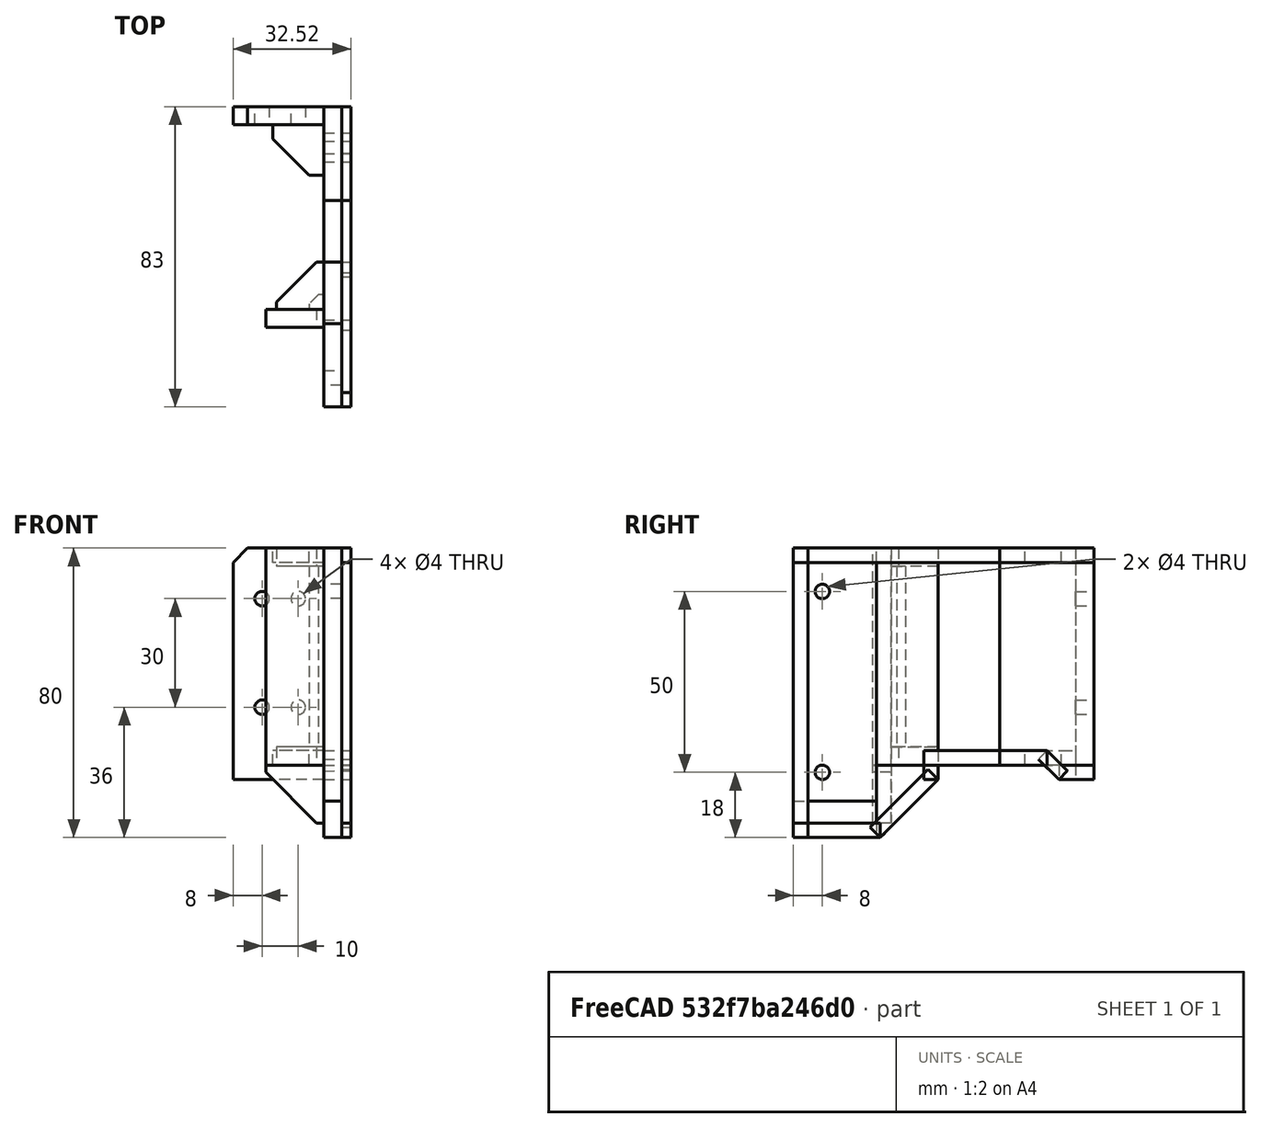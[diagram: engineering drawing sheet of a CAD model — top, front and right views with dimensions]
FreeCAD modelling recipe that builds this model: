
FCSTD DOCUMENT  (FreeCAD 0.20R29410 (Git))
Label: main_01
License: All rights reserved
LicenseURL: http://en.wikipedia.org/wiki/All_rights_reserved
objects: Part::Part2DObjectPython×33, Part::Extrusion×30, Part::Chamfer×8, Part::Cut×6
note: 77 computed .brp shape members not serialized (recipe doc carries the construction recipe); baked Part::Feature solids carry a one-line shape summary decoded from their .brp

FEATURE [Part::Part2DObjectPython] Rectangle  # Draft 2D object (typed FeaturePython)
  Area = 0
  ChamferSize = 0
  Columns = 1
  FilletRadius = 0
  Height = 70
  Length = 23
  MakeFace = false
  Placement = pos=(0,-40,0) rot=(0.57735,0.57735,0.57735;2.0944rad)
  Rows = 1
FEATURE [Part::Part2DObjectPython] Circle  # Draft 2D object (typed FeaturePython)
  Area = 0
  FirstAngle = 0
  LastAngle = 0
  MakeFace = false
  Placement = pos=(0,-32,58) rot=(0.57735,0.57735,0.57735;2.0944rad)
  Radius = 4
FEATURE [Part::Part2DObjectPython] Circle001  # Draft 2D object (typed FeaturePython)
  Area = 0
  FirstAngle = 0
  LastAngle = 0
  MakeFace = false
  Placement = pos=(0,-32,8) rot=(0.57735,0.57735,0.57735;2.0944rad)
  Radius = 4
FEATURE [Part::Part2DObjectPython] Rectangle001  # Draft 2D object (typed FeaturePython)
  Area = 0
  ChamferSize = 0
  Columns = 1
  FilletRadius = 0
  Height = 10
  Length = 23
  MakeFace = false
  Placement = pos=(0,-40,-10) rot=(0.57735,0.57735,0.57735;2.0944rad)
  Rows = 1
FEATURE [Part::Part2DObjectPython] Rectangle002  # Draft 2D object (typed FeaturePython)
  Area = 0
  ChamferSize = 0
  Columns = 1
  FilletRadius = 0
  Height = 20
  Length = 17
  MakeFace = false
  Placement = pos=(0,-17,-10) rot=(0.57735,0.57735,0.57735;2.0944rad)
  Rows = 1
FEATURE [Part::Part2DObjectPython] Rectangle003  # Draft 2D object (typed FeaturePython)
  Area = 0
  ChamferSize = 0
  Columns = 1
  FilletRadius = 0
  Height = 60
  Length = 17
  MakeFace = false
  Placement = pos=(0,0,10) rot=(0.57735,0.57735,0.57735;2.0944rad)
  Rows = 1
FEATURE [Part::Part2DObjectPython] Rectangle004  # Draft 2D object (typed FeaturePython)
  Area = 0
  ChamferSize = 0
  Columns = 1
  FilletRadius = 0
  Height = 60
  Length = 17
  MakeFace = false
  Placement = pos=(0,-17,10) rot=(0.57735,0.57735,0.57735;2.0944rad)
  Rows = 1
FEATURE [Part::Extrusion] Extrude
  Base = -> Rectangle
  Dir = (1,-2e-16,2e-16)
  DirMode = 2
  FaceMakerClass = Part::FaceMakerBullseye
  LengthFwd = 5
  LengthRev = 0
  Solid = true
  Symmetric = false
FEATURE [Part::Extrusion] Extrude001
  Base = -> Rectangle004
  Dir = (1,0,0)
  DirMode = 2
  FaceMakerClass = Part::FaceMakerBullseye
  LengthFwd = 5
  LengthRev = 0
  Solid = true
  Symmetric = false
FEATURE [Part::Extrusion] Extrude002
  Base = -> Rectangle003
  Dir = (1,-2e-16,2e-16)
  DirMode = 2
  FaceMakerClass = Part::FaceMakerBullseye
  LengthFwd = 5
  LengthRev = 0
  Solid = true
  Symmetric = false
FEATURE [Part::Extrusion] Extrude003
  Base = -> Rectangle001
  Dir = (1,-2e-16,2e-16)
  DirMode = 2
  FaceMakerClass = Part::FaceMakerBullseye
  LengthFwd = 5
  LengthRev = 0
  Solid = true
  Symmetric = false
FEATURE [Part::Extrusion] Extrude004
  Base = -> Rectangle002
  Dir = (1,-2e-16,2e-16)
  DirMode = 2
  FaceMakerClass = Part::FaceMakerBullseye
  LengthFwd = 5
  LengthRev = 0
  Solid = true
  Symmetric = false
FEATURE [Part::Chamfer] Chamfer
  Base = -> Extrude004
  Edges = 1 edges r=16: [Edge2]
FEATURE [Part::Part2DObjectPython] Rectangle005  # Draft 2D object (typed FeaturePython)
  Area = 0
  ChamferSize = 0
  Columns = 1
  FilletRadius = 0
  Height = 4
  Length = 57
  MakeFace = false
  Placement = pos=(5,-40,66) rot=(0.57735,0.57735,0.57735;2.0944rad)
  Rows = 1
FEATURE [Part::Part2DObjectPython] Rectangle006  # Draft 2D object (typed FeaturePython)
  Area = 0
  ChamferSize = 0
  Columns = 1
  FilletRadius = 0
  Height = 80
  Length = 4
  MakeFace = false
  Placement = pos=(5,-40,-10) rot=(0.57735,0.57735,0.57735;2.0944rad)
  Rows = 1
FEATURE [Part::Part2DObjectPython] Rectangle007  # Draft 2D object (typed FeaturePython)
  Area = 0
  ChamferSize = 0
  Columns = 1
  FilletRadius = 0
  Height = 4
  Length = 24
  MakeFace = false
  Placement = pos=(5,-40,-10) rot=(0.57735,0.57735,0.57735;2.0944rad)
  Rows = 1
FEATURE [Part::Part2DObjectPython] Rectangle008  # Draft 2D object (typed FeaturePython)
  Area = 0
  ChamferSize = 0
  Columns = 1
  FilletRadius = 0
  Height = 4
  Length = 22.6
  MakeFace = false
  Placement = pos=(5,-16,-10) rot=(0.678598,0.281085,0.678598;2.59356rad)
  Rows = 1
FEATURE [Part::Part2DObjectPython] Rectangle009  # Draft 2D object (typed FeaturePython)
  Area = 0
  ChamferSize = 0
  Columns = 1
  FilletRadius = 0
  Height = 4
  Length = 4
  MakeFace = false
  Placement = pos=(5,-4,6) rot=(0.57735,0.57735,0.57735;2.0944rad)
  Rows = 1
FEATURE [Part::Part2DObjectPython] Rectangle010  # Draft 2D object (typed FeaturePython)
  Area = 0
  ChamferSize = 0
  Columns = 1
  FilletRadius = 0
  Height = 4
  Length = 21
  MakeFace = false
  Placement = pos=(5,-4,10) rot=(0.57735,0.57735,0.57735;2.0944rad)
  Rows = 1
FEATURE [Part::Extrusion] Extrude005
  Base = -> Rectangle005
  Dir = (1,-2e-16,2e-16)
  DirMode = 2
  FaceMakerClass = Part::FaceMakerBullseye
  LengthFwd = 2.5
  LengthRev = 0
  Solid = true
  Symmetric = false
FEATURE [Part::Extrusion] Extrude006
  Base = -> Rectangle006
  Dir = (1,-2e-16,2e-16)
  DirMode = 2
  FaceMakerClass = Part::FaceMakerBullseye
  LengthFwd = 2.5
  LengthRev = 0
  Solid = true
  Symmetric = false
FEATURE [Part::Extrusion] Extrude007
  Base = -> Rectangle007
  Dir = (1,-2e-16,2e-16)
  DirMode = 2
  FaceMakerClass = Part::FaceMakerBullseye
  LengthFwd = 2.5
  LengthRev = 0
  Solid = true
  Symmetric = false
FEATURE [Part::Extrusion] Extrude008
  Base = -> Rectangle008
  Dir = (1,-2.79271e-06,1.15679e-06)
  DirMode = 2
  FaceMakerClass = Part::FaceMakerBullseye
  LengthFwd = 2.5
  LengthRev = 0
  Solid = true
  Symmetric = false
FEATURE [Part::Extrusion] Extrude009
  Base = -> Rectangle009
  Dir = (1,-2e-16,2e-16)
  DirMode = 2
  FaceMakerClass = Part::FaceMakerBullseye
  LengthFwd = 2.5
  LengthRev = 0
  Solid = true
  Symmetric = false
FEATURE [Part::Extrusion] Extrude010
  Base = -> Rectangle010
  Dir = (1,-2e-16,2e-16)
  DirMode = 2
  FaceMakerClass = Part::FaceMakerBullseye
  LengthFwd = 2.5
  LengthRev = 0
  Solid = true
  Symmetric = false
FEATURE [Part::Part2DObjectPython] Rectangle011  # Draft 2D object (typed FeaturePython)
  Area = 0
  ChamferSize = 0
  Columns = 1
  FilletRadius = 0
  Height = 60
  Length = 5.00266
  MakeFace = false
  Placement = pos=(6e-15,-13,10) rot=(0.57735,-0.57735,-0.57735;2.0944rad)
  Rows = 1
FEATURE [Part::Extrusion] Extrude011
  Base = -> Rectangle011
  Dir = (-1,2e-16,-2e-16)
  DirMode = 2
  FaceMakerClass = Part::FaceMakerBullseye
  LengthFwd = 16
  LengthRev = 0
  Solid = true
  Symmetric = false
FEATURE [Part::Part2DObjectPython] Rectangle012  # Draft 2D object (typed FeaturePython)
  Area = 0
  ChamferSize = 0
  Columns = 1
  FilletRadius = 0
  Height = 5
  Length = 13
  MakeFace = false
  Placement = pos=(0,0,63) rot=(0.57735,-0.57735,-0.57735;2.0944rad)
  Rows = 1
FEATURE [Part::Extrusion] Extrude012
  Base = -> Rectangle012
  Dir = (-1,-2e-16,2e-16)
  DirMode = 2
  FaceMakerClass = Part::FaceMakerBullseye
  LengthFwd = 13
  LengthRev = 0
  Solid = true
  Symmetric = false
FEATURE [Part::Chamfer] Chamfer001
  Base = -> Extrude012
  Edges = 1 edges r=11: [Edge12]
  Placement = pos=(0,0,2) rot=(0,0,1;0rad)
FEATURE [Part::Part2DObjectPython] Rectangle013  # Draft 2D object (typed FeaturePython)
  Area = 0
  ChamferSize = 0
  Columns = 1
  FilletRadius = 0
  Height = 5
  Length = 13
  MakeFace = false
  Placement = pos=(0,0,63) rot=(0.57735,-0.57735,-0.57735;2.0944rad)
  Rows = 1
FEATURE [Part::Extrusion] Extrude013
  Base = -> Rectangle013
  Dir = (-1,-2e-16,2e-16)
  DirMode = 2
  FaceMakerClass = Part::FaceMakerBullseye
  LengthFwd = 13
  LengthRev = 0
  Solid = true
  Symmetric = false
FEATURE [Part::Chamfer] Chamfer002
  Base = -> Extrude013
  Edges = 1 edges r=11: [Edge12]
  Placement = pos=(0,0,-53) rot=(0,0,1;0rad)
FEATURE [Part::Part2DObjectPython] Rectangle014  # Draft 2D object (typed FeaturePython)
  Area = 0
  ChamferSize = 0
  Columns = 1
  FilletRadius = 0
  Height = 49.9966
  Length = 4
  MakeFace = false
  Placement = pos=(0,-9,15) rot=(0.57735,-0.57735,-0.57735;2.0944rad)
  Rows = 1
FEATURE [Part::Extrusion] Extrude014
  Base = -> Rectangle014
  Dir = (-1,-2e-16,2e-16)
  DirMode = 2
  FaceMakerClass = Part::FaceMakerBullseye
  LengthFwd = 4
  LengthRev = 0
  Solid = true
  Symmetric = false
FEATURE [Part::Chamfer] Chamfer003
  Base = -> Extrude014
  Edges = 1 edges r=2.5: [Edge12]
FEATURE [Part::Part2DObjectPython] Rectangle015  # Draft 2D object (typed FeaturePython)
  Area = 0
  ChamferSize = 0
  Columns = 1
  FilletRadius = 0
  Height = 16
  Length = 5
  MakeFace = false
  Placement = pos=(0,-13,-6) rot=(0.57735,-0.57735,-0.57735;2.0944rad)
  Rows = 1
FEATURE [Part::Extrusion] Extrude015
  Base = -> Rectangle015
  Dir = (-1,-2e-16,2e-16)
  DirMode = 2
  FaceMakerClass = Part::FaceMakerBullseye
  LengthFwd = 16
  LengthRev = 0
  Solid = true
  Symmetric = false
FEATURE [Part::Chamfer] Chamfer004
  Base = -> Extrude015
  Edges = 1 edges r=14: [Edge4]
FEATURE [Part::Part2DObjectPython] Circle002  # Draft 2D object (typed FeaturePython)
  Area = 0
  FirstAngle = 0
  LastAngle = 0
  MakeFace = false
  Placement = pos=(0,-32,58) rot=(0.57735,0.57735,0.57735;2.0944rad)
  Radius = 2
FEATURE [Part::Part2DObjectPython] Circle003  # Draft 2D object (typed FeaturePython)
  Area = 0
  FirstAngle = 0
  LastAngle = 0
  MakeFace = false
  Placement = pos=(0,-32,8) rot=(0.57735,0.57735,0.57735;2.0944rad)
  Radius = 2
FEATURE [Part::Extrusion] Extrude016
  Base = -> Circle003
  Dir = (1,0,0)
  DirMode = 2
  FaceMakerClass = Part::FaceMakerBullseye
  LengthFwd = 5
  LengthRev = 0
  Solid = true
  Symmetric = false
FEATURE [Part::Extrusion] Extrude017
  Base = -> Circle002
  Dir = (1,0,0)
  DirMode = 2
  FaceMakerClass = Part::FaceMakerBullseye
  LengthFwd = 5
  LengthRev = 0
  Solid = true
  Symmetric = false
FEATURE [Part::Cut] Cut
  Base = -> Extrude
  Tool = -> Extrude016
FEATURE [Part::Cut] Cut001
  Base = -> Cut
  Tool = -> Extrude017
FEATURE [Part::Part2DObjectPython] Rectangle016  # Draft 2D object (typed FeaturePython)
  Area = 300
  ChamferSize = 0
  Columns = 1
  FilletRadius = 0
  Height = 60
  Length = 5
  MakeFace = true
  Placement = pos=(5,17,10) rot=(0,0.707107,0.707107;3.14159rad)
  Rows = 1
FEATURE [Part::Extrusion] Extrude018
  Base = -> Rectangle016
  Dir = (1e-16,1,0)
  DirMode = 2
  FaceMakerClass = Part::FaceMakerBullseye
  LengthFwd = 26
  LengthRev = 0
  Solid = false
  Symmetric = false
FEATURE [Part::Part2DObjectPython] Rectangle017  # Draft 2D object (typed FeaturePython)
  Area = 10
  ChamferSize = 0
  Columns = 1
  FilletRadius = 0
  Height = 4
  Length = 2.5
  MakeFace = true
  Placement = pos=(7.5,17,66) rot=(0,0.707107,0.707107;3.14159rad)
  Rows = 1
FEATURE [Part::Part2DObjectPython] Rectangle018  # Draft 2D object (typed FeaturePython)
  Area = 10
  ChamferSize = 0
  Columns = 1
  FilletRadius = 0
  Height = 4
  Length = 2.5
  MakeFace = true
  Placement = pos=(7.5,17,10) rot=(0,0.707107,0.707107;3.14159rad)
  Rows = 1
FEATURE [Part::Extrusion] Extrude019
  Base = -> Rectangle017
  Dir = (2e-16,1,-2e-16)
  DirMode = 2
  FaceMakerClass = Part::FaceMakerBullseye
  LengthFwd = 26
  LengthRev = 0
  Solid = false
  Symmetric = false
FEATURE [Part::Extrusion] Extrude020
  Base = -> Rectangle018
  Dir = (1e-16,1,0)
  DirMode = 2
  FaceMakerClass = Part::FaceMakerBullseye
  LengthFwd = 13
  LengthRev = 0
  Solid = false
  Symmetric = false
FEATURE [Part::Part2DObjectPython] Rectangle019  # Draft 2D object (typed FeaturePython)
  Area = 38.4
  ChamferSize = 0
  Columns = 1
  FilletRadius = 0
  Height = 4
  Length = 9.6
  MakeFace = true
  Placement = pos=(5,33.4,6) rot=(0.57735,0.57735,0.57735;2.0944rad)
  Rows = 1
FEATURE [Part::Part2DObjectPython] Rectangle020  # Draft 2D object (typed FeaturePython)
  Area = 26.4
  ChamferSize = 0
  Columns = 1
  FilletRadius = 0
  Height = 3.3
  Length = 8
  MakeFace = true
  Placement = pos=(5,27.7,11.65) rot=(-0.360216,-0.860516,-0.360216;4.56543rad)
  Rows = 1
FEATURE [Part::Extrusion] Extrude021
  Base = -> Rectangle020
  Dir = (0.999997,-0.000972878,0.00232728)
  DirMode = 2
  FaceMakerClass = Part::FaceMakerBullseye
  LengthFwd = 2.5
  LengthRev = 5
  Solid = false
  Symmetric = false
FEATURE [Part::Extrusion] Extrude022
  Base = -> Rectangle019
  Dir = (1,-2e-16,2e-16)
  DirMode = 2
  FaceMakerClass = Part::FaceMakerBullseye
  LengthFwd = 2.5
  LengthRev = 5
  Solid = false
  Symmetric = false
FEATURE [Part::Part2DObjectPython] Rectangle021  # Draft 2D object (typed FeaturePython)
  Area = 320
  ChamferSize = 0
  Columns = 1
  FilletRadius = 0
  Height = 64
  Length = 5
  MakeFace = true
  Placement = pos=(0,38,6) rot=(0.57735,0.57735,0.57735;2.0944rad)
  Rows = 1
FEATURE [Part::Extrusion] Extrude023
  Base = -> Rectangle021
  Dir = (1,-2e-16,2e-16)
  DirMode = 2
  FaceMakerClass = Part::FaceMakerBullseye
  LengthFwd = -25
  LengthRev = 0
  Solid = false
  Symmetric = false
FEATURE [Part::Chamfer] Chamfer005
  Base = -> Extrude023
  Edges = 1 edges r=4: [Edge10]
FEATURE [Part::Part2DObjectPython] Rectangle022  # Draft 2D object (typed FeaturePython)
  Area = 56
  ChamferSize = 0
  Columns = 1
  FilletRadius = 0
  Height = 4
  Length = 14
  MakeFace = true
  Placement = pos=(0,38,66) rot=(-0.57735,0.57735,0.57735;4.18879rad)
  Rows = 1
FEATURE [Part::Extrusion] Extrude024
  Base = -> Rectangle022
  Dir = (-1,2e-16,-2e-16)
  DirMode = 2
  FaceMakerClass = Part::FaceMakerBullseye
  LengthFwd = 14
  LengthRev = 0
  Solid = false
  Symmetric = false
FEATURE [Part::Chamfer] Chamfer006
  Base = -> Extrude024
  Edges = 1 edges r=10: [Edge7]
FEATURE [Part::Part2DObjectPython] Rectangle023  # Draft 2D object (typed FeaturePython)
  Area = 56
  ChamferSize = 0
  Columns = 1
  FilletRadius = 0
  Height = 4
  Length = 14
  MakeFace = true
  Placement = pos=(0,38,66) rot=(0.57735,-0.57735,-0.57735;2.0944rad)
  Rows = 1
FEATURE [Part::Extrusion] Extrude025
  Base = -> Rectangle023
  Dir = (-1,2e-16,-2e-16)
  DirMode = 2
  FaceMakerClass = Part::FaceMakerBullseye
  LengthFwd = 14
  LengthRev = 0
  Solid = false
  Symmetric = false
FEATURE [Part::Chamfer] Chamfer007
  Base = -> Extrude025
  Edges = 1 edges r=10: [Edge7]
  Placement = pos=(0,0,-56) rot=(0,0,1;0rad)
FEATURE [Part::Part2DObjectPython] Rectangle071  # Draft 2D object (typed FeaturePython)
  Area = 140
  ChamferSize = 0
  Columns = 1
  FilletRadius = 0
  Height = 20
  Length = 7
  MakeFace = true
  Placement = pos=(-7,43,6) rot=(1,0,0;1.5708rad)
  Rows = 1
FEATURE [Part::Part2DObjectPython] Circle004  # Draft 2D object (typed FeaturePython)
  Area = 12.5664
  FirstAngle = 0
  LastAngle = 0
  MakeFace = true
  Placement = pos=(-17,43,26) rot=(1,0,0;1.5708rad)
  Radius = 2
FEATURE [Part::Part2DObjectPython] Circle005  # Draft 2D object (typed FeaturePython)
  Area = 12.5664
  FirstAngle = 0
  LastAngle = 0
  MakeFace = true
  Placement = pos=(-17,43,56) rot=(1,0,0;1.5708rad)
  Radius = 2
FEATURE [Part::Part2DObjectPython] Circle006  # Draft 2D object (typed FeaturePython)
  Area = 12.5664
  FirstAngle = 0
  LastAngle = 0
  MakeFace = true
  Placement = pos=(-7,43,56) rot=(1,0,0;1.5708rad)
  Radius = 2
FEATURE [Part::Part2DObjectPython] Circle007  # Draft 2D object (typed FeaturePython)
  Area = 12.5664
  FirstAngle = 0
  LastAngle = 0
  MakeFace = true
  Placement = pos=(-7,43,26) rot=(1,0,0;1.5708rad)
  Radius = 2
FEATURE [Part::Extrusion] Extrude026
  Base = -> Circle004
  Dir = (0,-1,2e-16)
  DirMode = 2
  FaceMakerClass = Part::FaceMakerBullseye
  LengthFwd = 5
  LengthRev = 0
  Solid = false
  Symmetric = false
FEATURE [Part::Extrusion] Extrude027
  Base = -> Circle007
  Dir = (0,-1,2e-16)
  DirMode = 2
  FaceMakerClass = Part::FaceMakerBullseye
  LengthFwd = 5
  LengthRev = 0
  Solid = false
  Symmetric = false
FEATURE [Part::Extrusion] Extrude028
  Base = -> Circle006
  Dir = (0,-1,2e-16)
  DirMode = 2
  FaceMakerClass = Part::FaceMakerBullseye
  LengthFwd = 5
  LengthRev = 0
  Solid = false
  Symmetric = false
FEATURE [Part::Extrusion] Extrude029
  Base = -> Circle005
  Dir = (0,-1,2e-16)
  DirMode = 2
  FaceMakerClass = Part::FaceMakerBullseye
  LengthFwd = 5
  LengthRev = 0
  Solid = false
  Symmetric = false
FEATURE [Part::Cut] Cut002
  Base = -> Chamfer005
  Tool = -> Extrude026
FEATURE [Part::Cut] Cut003
  Base = -> Cut002
  Tool = -> Extrude027
FEATURE [Part::Cut] Cut004
  Base = -> Cut003
  Tool = -> Extrude028
FEATURE [Part::Cut] Cut005
  Base = -> Cut004
  Tool = -> Extrude029
